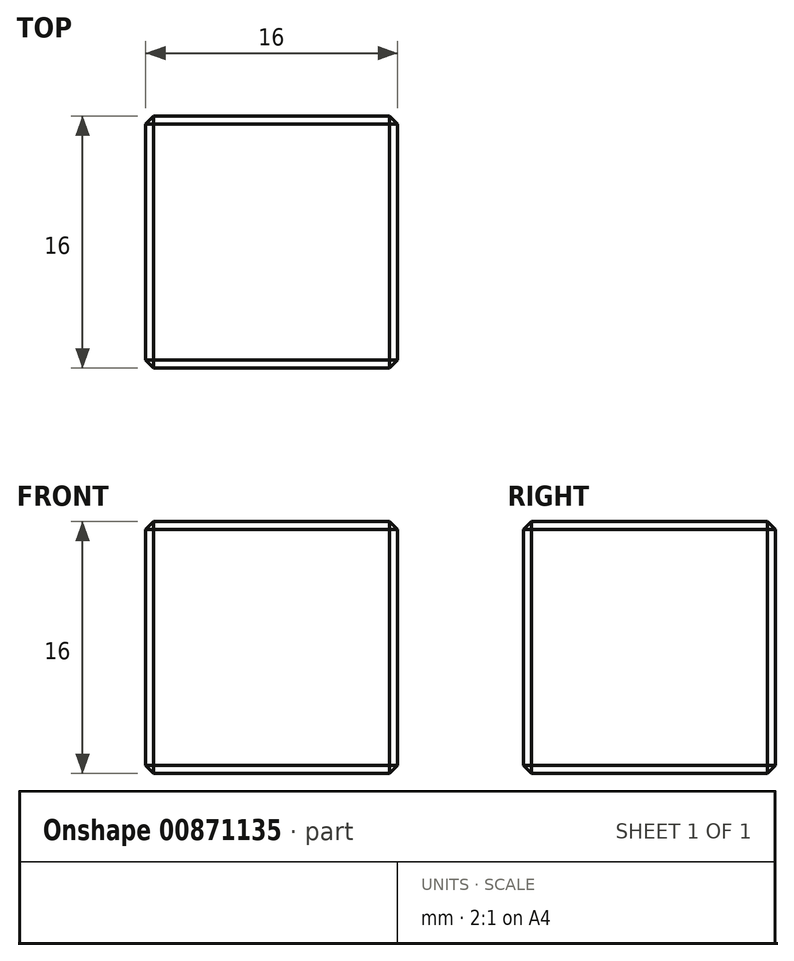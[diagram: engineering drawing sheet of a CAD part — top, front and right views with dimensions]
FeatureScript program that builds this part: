
annotation { "Feature Type Name" : "Feature", "Feature Type Description" : "" }
export const myFeature = defineFeature(function(context is Context, id is Id, definition is map)
    precondition{}
    {
        {
            var Q0;
            Q0=qCreatedBy(makeId("Top.planeOp"),FACE);
            var sketch = newSketch(context, id + "F0", { "sketchPlane" : qUnion([Q0])});
            skLineSegment(sketch, "E0.bottom", {"start": v(8, -8) * mm, "end": v(-8, -8) * mm});
            skLineSegment(sketch, "E0.top", {"start": v(8, 8) * mm, "end": v(-8, 8) * mm});
            skLineSegment(sketch, "E0.left", {"start": v(8, -8) * mm, "end": v(8, 8) * mm});
            skLineSegment(sketch, "E0.right", {"start": v(-8, -8) * mm, "end": v(-8, 8) * mm});
            skPoint(sketch, "E0.middle", {"position": v(0, 0) * mm});
            skSolve(sketch);
        }
        {
            var Q0;
            Q0=makeQuery(id+"F0.imprint","IMPRINT",FACE,{"disambiguationData":[TD([[makeQuery(id+"F0.imprint","IMPRINT",EDGE,{"derivedFrom":sQuery(id+"F0.wireOp",EDGE,"E0.bottom")}),-1.0]])]});
            extrude(context, id + "F1", {"entities" : qUnion([Q0]), "endBound" : BoundingType.SYMMETRIC, "depth" : 16 * mm, "offsetDistance" : 25.4 * mm});
        }
        {
            var Q0;
            Q0=makeQuery(id+"F1.opExtrude","CAP_EDGE",EDGE,{"disambiguationData":[OSD([sQuery(id+"F0.wireOp",EDGE,"E0.top")])],"isStart":false});
            var Q1;
            Q1=makeQuery(id+"F1.opExtrude","SWEPT_EDGE",EDGE,{"disambiguationData":[OSD([sQuery(id+"F0.wireOp",EDGE,"E0.top"),sQuery(id+"F0.wireOp",EDGE,"E0.left")])]});
            var Q2;
            Q2=makeQuery(id+"F1.opExtrude","CAP_EDGE",EDGE,{"disambiguationData":[OSD([sQuery(id+"F0.wireOp",EDGE,"E0.top")])],"isStart":true});
            var Q3;
            Q3=makeQuery(id+"F1.opExtrude","SWEPT_EDGE",EDGE,{"disambiguationData":[OSD([sQuery(id+"F0.wireOp",EDGE,"E0.top"),sQuery(id+"F0.wireOp",EDGE,"E0.right")])]});
            var Q4;
            Q4=makeQuery(id+"F1.opExtrude","CAP_EDGE",EDGE,{"disambiguationData":[OSD([sQuery(id+"F0.wireOp",EDGE,"E0.right")])],"isStart":true});
            var Q5;
            Q5=makeQuery(id+"F1.opExtrude","CAP_EDGE",EDGE,{"disambiguationData":[OSD([sQuery(id+"F0.wireOp",EDGE,"E0.right")])],"isStart":false});
            var Q6;
            Q6=makeQuery(id+"F1.opExtrude","CAP_EDGE",EDGE,{"disambiguationData":[OSD([sQuery(id+"F0.wireOp",EDGE,"E0.bottom")])],"isStart":false});
            var Q7;
            Q7=makeQuery(id+"F1.opExtrude","SWEPT_EDGE",EDGE,{"disambiguationData":[OSD([sQuery(id+"F0.wireOp",EDGE,"E0.bottom"),sQuery(id+"F0.wireOp",EDGE,"E0.right")])]});
            var Q8;
            Q8=makeQuery(id+"F1.opExtrude","SWEPT_EDGE",EDGE,{"disambiguationData":[OSD([sQuery(id+"F0.wireOp",EDGE,"E0.bottom"),sQuery(id+"F0.wireOp",EDGE,"E0.left")])]});
            var Q9;
            Q9=makeQuery(id+"F1.opExtrude","CAP_EDGE",EDGE,{"disambiguationData":[OSD([sQuery(id+"F0.wireOp",EDGE,"E0.left")])],"isStart":true});
            var Q10;
            Q10=makeQuery(id+"F1.opExtrude","CAP_EDGE",EDGE,{"disambiguationData":[OSD([sQuery(id+"F0.wireOp",EDGE,"E0.left")])],"isStart":false});
            var Q11;
            Q11=makeQuery(id+"F1.opExtrude","CAP_EDGE",EDGE,{"disambiguationData":[OSD([sQuery(id+"F0.wireOp",EDGE,"E0.bottom")])],"isStart":true});
            chamfer(context, id + "F2", {"entities" : qUnion([Q0, Q1, Q2, Q3, Q4, Q5, Q6, Q7, Q8, Q9, Q10, Q11]), "width" : .5 * mm, "tangentPropagation" : true});
        }
    });
